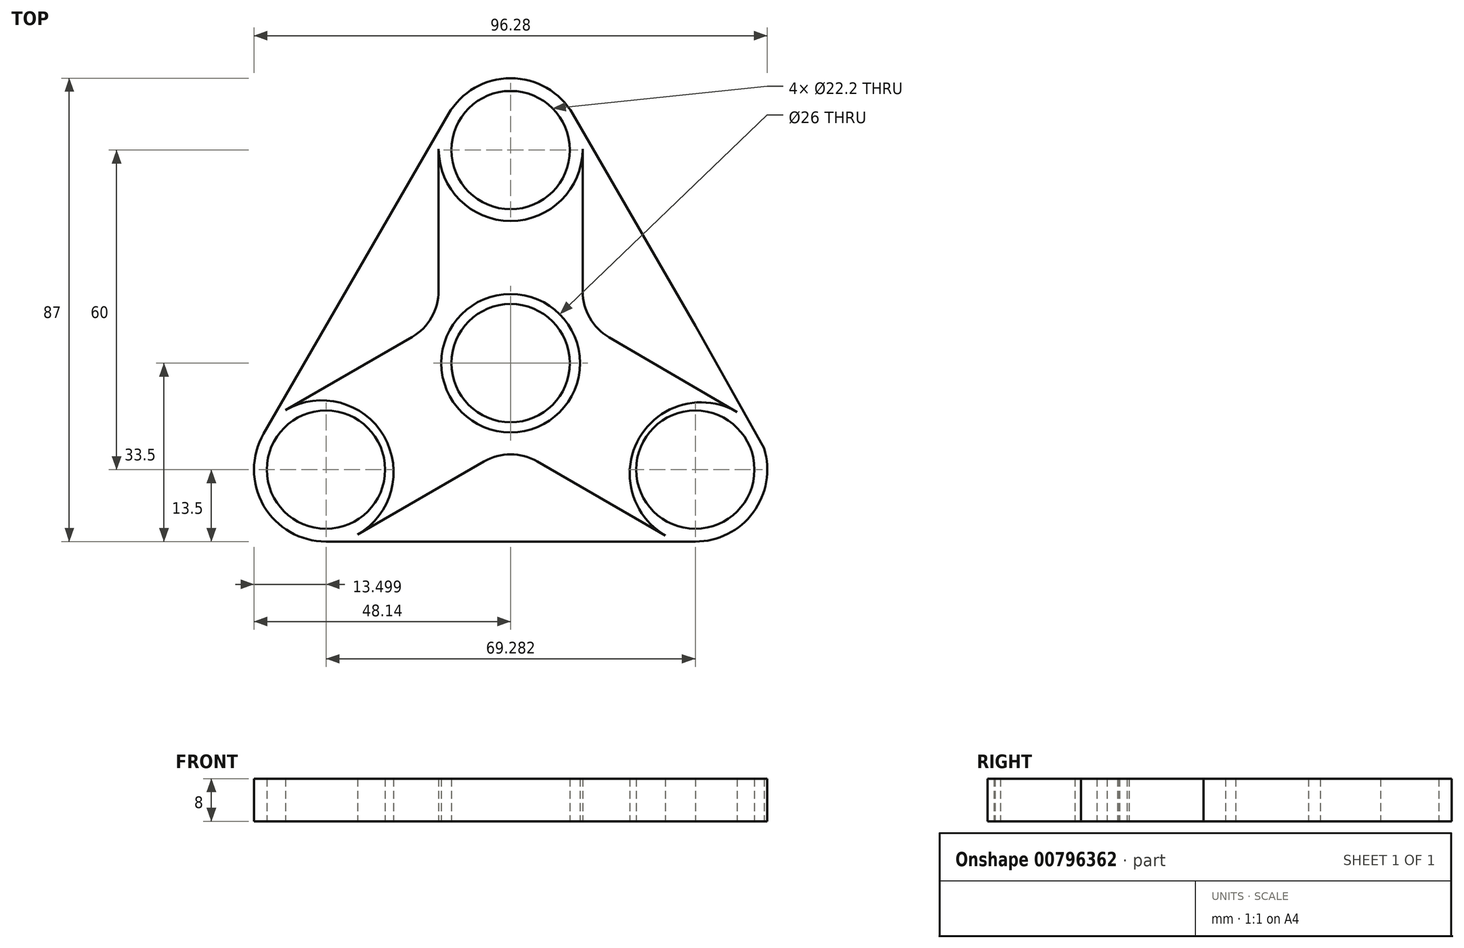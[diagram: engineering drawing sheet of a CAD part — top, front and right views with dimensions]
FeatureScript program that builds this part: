
annotation { "Feature Type Name" : "Feature", "Feature Type Description" : "" }
export const myFeature = defineFeature(function(context is Context, id is Id, definition is map)
    precondition{}
    {
        {
            var Q0;
            Q0=qCreatedBy(makeId("Top.planeOp"),FACE);
            var sketch = newSketch(context, id + "F0", { "sketchPlane" : qUnion([Q0])});
            skCircle(sketch, "E0", {"center": v(0, 0) * mm, "radius": 13.5 * mm});
            skCircle(sketch, "E1", {"center": v(0, 40) * mm, "radius": 13.5 * mm});
            skCircle(sketch, "E2.1.0", {"center": v(-34.64, -20) * mm, "radius": 13.5 * mm});
            skCircle(sketch, "E2.2.0", {"center": v(34.64, -20) * mm, "radius": 13.5 * mm});
            skCircle(sketch, "E3", {"center": v(0, 40) * mm, "radius": 11.1 * mm});
            skCircle(sketch, "E4", {"center": v(34.64, -20) * mm, "radius": 11.1 * mm});
            skCircle(sketch, "E5", {"center": v(-34.64, -20) * mm, "radius": 11.1 * mm});
            skCircle(sketch, "E6", {"center": v(0, 0) * mm, "radius": 11.1 * mm});
            skLineSegment(sketch, "E7", {"start": v(-34.64, 7) * mm, "end": v(-23.17, 26.88) * mm});
            skLineSegment(sketch, "E8", {"start": v(23.17, 26.88) * mm, "end": v(34.64, 7) * mm});
            skLineSegment(sketch, "E9", {"start": v(-11.26, -33.5) * mm, "end": v(11.7, -33.5) * mm});
            skPoint(sketch, "E10.orphan", {"position": v(-46.33, -13.25) * mm});
            skPoint(sketch, "E11.orphan", {"position": v(34.64, -33.5) * mm});
            skPoint(sketch, "E12.orphan", {"position": v(-11.7, 46.75) * mm});
            skPoint(sketch, "E13.orphan", {"position": v(11.7, 46.75) * mm});
            skLineSegment(sketch, "E14", {"start": v(-23.17, 26.88) * mm, "end": v(-11.7, 46.75) * mm});
            skLineSegment(sketch, "E15", {"start": v(-34.64, 7) * mm, "end": v(-46.33, -13.25) * mm});
            skLineSegment(sketch, "E16", {"start": v(11.7, 46.75) * mm, "end": v(23.17, 26.88) * mm});
            skLineSegment(sketch, "E17", {"start": v(34.64, 7) * mm, "end": v(47.54, -16.01) * mm});
            skLineSegment(sketch, "E18", {"start": v(11.7, -33.5) * mm, "end": v(34.64, -33.5) * mm});
            skLineSegment(sketch, "E19", {"start": v(-11.26, -33.5) * mm, "end": v(-34.64, -33.5) * mm});
            skSolve(sketch);
        }
        {
            var Q0;
            Q0=qCreatedBy(makeId("Top.planeOp"),FACE);
            var sketch = newSketch(context, id + "F1", { "sketchPlane" : qUnion([Q0])});
            skLineSegment(sketch, "E20", {"start": v(-42.2, -8.78) * mm, "end": v(-18.5, 4.9) * mm});
            skLineSegment(sketch, "E21", {"start": v(-28.7, -32.16) * mm, "end": v(-5, -18.48) * mm});
            skLineSegment(sketch, "E22", {"start": v(18.46, 4.86) * mm, "end": v(42.5, -9.18) * mm});
            skLineSegment(sketch, "E23", {"start": v(29.04, -32.36) * mm, "end": v(5, -18.48) * mm});
            skLineSegment(sketch, "E24", {"start": v(-13.5, 40.18) * mm, "end": v(-13.5, 13.57) * mm});
            skLineSegment(sketch, "E25", {"start": v(13.5, 40.18) * mm, "end": v(13.5, 13.5) * mm});
            skPoint(sketch, "E26.orphan", {"position": v(-13.5, 0) * mm});
            skPoint(sketch, "E27.orphan", {"position": v(13.5, 0) * mm});
            skPoint(sketch, "E28.visualSharp", {"position": v(-13.5, 7.8) * mm});
            skArc(sketch, "E28.filletArc", {"start": v(-18.5, 4.9) * mm, "mid": v(-14.84, 8.57) * mm, "end": v(-13.5, 13.57) * mm});
            skPoint(sketch, "E29.visualSharp", {"position": v(13.5, 7.75) * mm});
            skArc(sketch, "E29.filletArc", {"start": v(13.5, 13.5) * mm, "mid": v(14.83, 8.51) * mm, "end": v(18.46, 4.86) * mm});
            skPoint(sketch, "E30.visualSharp", {"position": v(0, -15.59) * mm});
            skArc(sketch, "E30.filletArc", {"start": v(5, -18.48) * mm, "mid": v(0, -17.14) * mm, "end": v(-5, -18.48) * mm});
            skArc(sketch, "E31", {"start": v(-13.5, 40.18) * mm, "mid": v(0, 26.68) * mm, "end": v(13.5, 40.18) * mm});
            skPoint(sketch, "E31.third.point", {"position": v(0, 53.68) * mm});
            skPoint(sketch, "E31.third.point.positionSnap0", {"position": v(0, 40.18) * mm});
            skArc(sketch, "E32", {"start": v(42.5, -9.18) * mm, "mid": v(24.15, -14.02) * mm, "end": v(29.04, -32.36) * mm});
            skPoint(sketch, "E32.third.point", {"position": v(47.1, -27.85) * mm});
            skArc(sketch, "E33", {"start": v(-28.7, -32.16) * mm, "mid": v(-23.77, -13.72) * mm, "end": v(-42.2, -8.78) * mm});
            skPoint(sketch, "E33.third.point", {"position": v(-48.06, -25.32) * mm});
            skPoint(sketch, "E33.third.point.positionSnap0", {"position": v(-16.85, -25.32) * mm});
            skCircle(sketch, "E34", {"center": v(0, 0) * mm, "radius": 13 * mm});
            skSolve(sketch);
        }
        {
            var Q0;
            Q0=makeQuery(id+"F1.imprint","IMPRINT",FACE,{"disambiguationData":[TD([[makeQuery(id+"F1.imprint","IMPRINT",EDGE,{"derivedFrom":sQuery(id+"F1.wireOp",EDGE,"E20")}),-1.0]])]});
            extrude(context, id + "F2", {"entities" : qUnion([Q0]), "endBound" : BoundingType.SYMMETRIC, "depth" : 8 * mm, "offsetDistance" : 25 * mm});
        }
        {
            var Q0;
            Q0=makeQuery(id+"F0.imprint","IMPRINT",FACE,{"disambiguationData":[TD([[makeQuery(id+"F0.imprint","IMPRINT",EDGE,{"derivedFrom":sQuery(id+"F0.wireOp",EDGE,"E1")}),1.0]])]});
            var Q1;
            Q1=makeQuery(id+"F0.imprint","IMPRINT",FACE,{"disambiguationData":[TD([[makeQuery(id+"F0.imprint","IMPRINT",EDGE,{"derivedFrom":sQuery(id+"F0.wireOp",EDGE,"E2.2.0")}),1.0]])]});
            var Q2;
            Q2=makeQuery(id+"F0.imprint","IMPRINT",FACE,{"disambiguationData":[TD([[makeQuery(id+"F0.imprint","IMPRINT",EDGE,{"derivedFrom":sQuery(id+"F0.wireOp",EDGE,"E2.1.0")}),1.0]])]});
            var Q3;
            Q3=makeQuery(id+"F0.imprint","IMPRINT",FACE,{"disambiguationData":[TD([[makeQuery(id+"F0.imprint","IMPRINT",EDGE,{"derivedFrom":sQuery(id+"F0.wireOp",EDGE,"E0")}),1.0]])]});
            var Q4;
            Q4=makeQuery(id+"F0.imprint","IMPRINT",FACE,{"disambiguationData":[TD([[makeQuery(id+"F0.imprint","IMPRINT",EDGE,{"derivedFrom":sQuery(id+"F0.wireOp",EDGE,"E0")}),-1.0]])]});
            extrude(context, id + "F3", {"entities" : qUnion([Q0, Q1, Q2, Q3, Q4]), "endBound" : BoundingType.SYMMETRIC, "depth" : 8 * mm, "offsetDistance" : 25 * mm});
        }
    });
